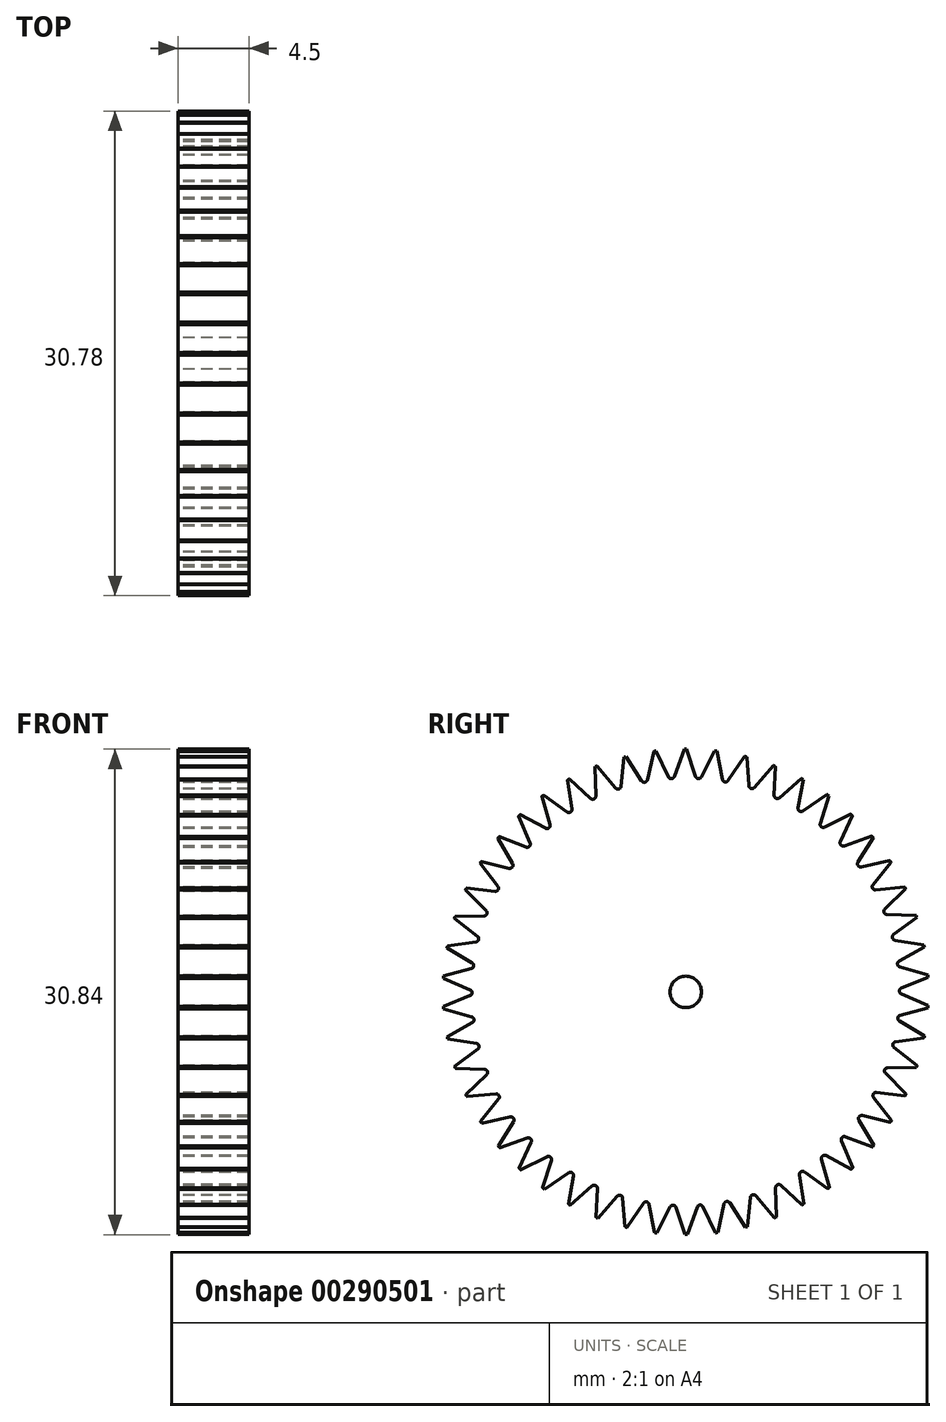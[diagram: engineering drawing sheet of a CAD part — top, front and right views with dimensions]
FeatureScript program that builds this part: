
annotation { "Feature Type Name" : "Feature", "Feature Type Description" : "" }
export const myFeature = defineFeature(function(context is Context, id is Id, definition is map)
    precondition{}
    {
        {
            var Q0;
            Q0=qCreatedBy(makeId("Top.planeOp"),FACE);
            var sketch = newSketch(context, id + "F0", { "sketchPlane" : qUnion([Q0])});
            skLineSegment(sketch, "E0", {"start": v(0, 3.41) * mm, "end": v(0, -3.75) * mm, "construction": true});
            skLineSegment(sketch, "E1", {"start": v(0, 9.42) * mm, "end": v(2.25, 9.42) * mm});
            skLineSegment(sketch, "E2", {"start": v(2.25, 9.42) * mm, "end": v(2.25, 4.42) * mm});
            skLineSegment(sketch, "E3", {"start": v(2.25, 4.42) * mm, "end": v(2.25, 4.42) * mm});
            skLineSegment(sketch, "E4", {"start": v(2.25, 4.42) * mm, "end": v(2.25, 0) * mm});
            skLineSegment(sketch, "E5", {"start": v(2.25, 0) * mm, "end": v(2.25, 0) * mm});
            skLineSegment(sketch, "E6", {"start": v(2.25, 0) * mm, "end": v(2.25, -5) * mm});
            skLineSegment(sketch, "E7", {"start": v(2.25, -5) * mm, "end": v(0, -5) * mm});
            skLineSegment(sketch, "E8.MirrorCS", {"start": v(-2.25, 0) * mm, "end": v(-2.25, 0) * mm});
            skLineSegment(sketch, "E9.MirrorCS", {"start": v(0, 9.42) * mm, "end": v(-2.25, 9.42) * mm});
            skLineSegment(sketch, "E10.MirrorCS", {"start": v(-2.25, -5) * mm, "end": v(0, -5) * mm});
            skLineSegment(sketch, "E11.MirrorCS", {"start": v(-2.25, 0) * mm, "end": v(-2.25, -5) * mm});
            skLineSegment(sketch, "E12.MirrorCS", {"start": v(-2.25, 9.42) * mm, "end": v(-2.25, 4.42) * mm});
            skLineSegment(sketch, "E13.MirrorCS", {"start": v(-2.25, 4.42) * mm, "end": v(-2.25, 0) * mm});
            skLineSegment(sketch, "E14.MirrorCS", {"start": v(-2.25, 4.42) * mm, "end": v(-2.25, 4.42) * mm});
            skLineSegment(sketch, "E15", {"start": v(-2.96, -6) * mm, "end": v(4.6, -6) * mm, "construction": true});
            skLineSegment(sketch, "E16.MirrorCS", {"start": v(-2.25, -12) * mm, "end": v(-2.25, -12) * mm});
            skLineSegment(sketch, "E17.MirrorCS", {"start": v(2.25, -12) * mm, "end": v(2.25, -12) * mm});
            skLineSegment(sketch, "E18.MirrorCS", {"start": v(-2.25, -16.42) * mm, "end": v(-2.25, -16.42) * mm});
            skLineSegment(sketch, "E19.MirrorCS", {"start": v(-2.25, -16.42) * mm, "end": v(-2.25, -12) * mm});
            skLineSegment(sketch, "E20.MirrorCS", {"start": v(-2.25, -21.42) * mm, "end": v(-2.25, -16.42) * mm});
            skLineSegment(sketch, "E21.MirrorCS", {"start": v(-2.25, -12) * mm, "end": v(-2.25, -7) * mm});
            skLineSegment(sketch, "E22.MirrorCS", {"start": v(-2.25, -7) * mm, "end": v(0, -7) * mm});
            skLineSegment(sketch, "E23.MirrorCS", {"start": v(0, -21.42) * mm, "end": v(-2.25, -21.42) * mm});
            skLineSegment(sketch, "E24.MirrorCS", {"start": v(2.25, -7) * mm, "end": v(0, -7) * mm});
            skLineSegment(sketch, "E25.MirrorCS", {"start": v(2.25, -21.42) * mm, "end": v(2.25, -16.42) * mm});
            skLineSegment(sketch, "E26.MirrorCS", {"start": v(2.25, -16.42) * mm, "end": v(2.25, -16.42) * mm});
            skLineSegment(sketch, "E27.MirrorCS", {"start": v(2.25, -12) * mm, "end": v(2.25, -7) * mm});
            skLineSegment(sketch, "E28.MirrorCS", {"start": v(2.25, -16.42) * mm, "end": v(2.25, -12) * mm});
            skLineSegment(sketch, "E29.MirrorCS", {"start": v(0, -21.42) * mm, "end": v(2.25, -21.42) * mm});
            skSolve(sketch);
        }
        {
            var Q0;
            Q0=makeQuery(id+"F0.imprint","IMPRINT",FACE,{"disambiguationData":[TD([[makeQuery(id+"F0.imprint","IMPRINT",EDGE,{"derivedFrom":sQuery(id+"F0.wireOp",EDGE,"E1")}),-1.0]])]});
            var Q1;
            Q1=sQuery(id+"F0.wireOp",EDGE,"E14.MirrorCS");
            var Q2;
            Q2=sQuery(id+"F0.wireOp",EDGE,"E13.MirrorCS");
            var Q3;
            Q3=sQuery(id+"F0.wireOp",EDGE,"E2");
            var Q4;
            Q4=sQuery(id+"F0.wireOp",EDGE,"E3");
            var Q5;
            Q5=sQuery(id+"F0.wireOp",EDGE,"E1");
            var Q6;
            Q6=sQuery(id+"F0.wireOp",EDGE,"E4");
            var Q7;
            Q7=sQuery(id+"F0.wireOp",EDGE,"E7");
            var Q8;
            Q8=sQuery(id+"F0.wireOp",EDGE,"E9.MirrorCS");
            var Q9;
            Q9=sQuery(id+"F0.wireOp",EDGE,"E10.MirrorCS");
            var Q10;
            Q10=sQuery(id+"F0.wireOp",EDGE,"E12.MirrorCS");
            var Q11;
            Q11=sQuery(id+"F0.wireOp",EDGE,"E5");
            var Q12;
            Q12=sQuery(id+"F0.wireOp",EDGE,"E6");
            var Q13;
            Q13=sQuery(id+"F0.wireOp",EDGE,"E8.MirrorCS");
            var Q14;
            Q14=sQuery(id+"F0.wireOp",EDGE,"E11.MirrorCS");
            var Q15;
            Q15=sQuery(id+"F0.wireOp",EDGE,"E15");
            revolve(context, id + "F1", {"entities" : qUnion([Q0]), "surfaceEntities" : qUnion([Q1, Q2, Q3, Q4, Q5, Q6, Q7, Q8, Q9, Q10, Q11, Q12, Q13, Q14]), "axis" : qUnion([Q15]), "revolveType" : RevolveType.FULL});
        }
        {
            var Q0;
            Q0=makeQuery(id+"F1.opRevolve","SWEPT_FACE",FACE,{"disambiguationData":[OSD([sQuery(id+"F0.wireOp",EDGE,"E12.MirrorCS")])]});
            var sketch = newSketch(context, id + "F2", { "sketchPlane" : qUnion([Q0])});
            skCircle(sketch, "E30.0", {"center": v(6, 0) * mm, "radius": 15.42 * mm});
            skCircle(sketch, "E30.1", {"center": v(6.5, 0) * mm, "radius": 10.92 * mm});
            skCircle(sketch, "E30.2", {"center": v(6, 0) * mm, "radius": 1 * mm});
            skLineSegment(sketch, "E31", {"start": v(6, 0) * mm, "end": v(21.39, 0.94) * mm});
            skLineSegment(sketch, "E32.1.0", {"start": v(6, 0) * mm, "end": v(21.15, 2.86) * mm});
            skLineSegment(sketch, "E32.2.0", {"start": v(6, 0) * mm, "end": v(20.67, 4.74) * mm});
            skLineSegment(sketch, "E32.3.0", {"start": v(6, 0) * mm, "end": v(19.96, 6.54) * mm});
            skLineSegment(sketch, "E32.4.0", {"start": v(6, 0) * mm, "end": v(19.03, 8.24) * mm});
            skLineSegment(sketch, "E32.5.0", {"start": v(6, 0) * mm, "end": v(17.9, 9.8) * mm});
            skLineSegment(sketch, "E32.6.0", {"start": v(6, 0) * mm, "end": v(16.57, 11.22) * mm});
            skLineSegment(sketch, "E32.7.0", {"start": v(6, 0) * mm, "end": v(15.08, 12.46) * mm});
            skLineSegment(sketch, "E32.8.0", {"start": v(6, 0) * mm, "end": v(13.45, 13.5) * mm});
            skLineSegment(sketch, "E32.9.0", {"start": v(6, 0) * mm, "end": v(11.7, 14.32) * mm});
            skLineSegment(sketch, "E32.10.0", {"start": v(6, 0) * mm, "end": v(9.86, 14.92) * mm});
            skLineSegment(sketch, "E32.11.0", {"start": v(6, 0) * mm, "end": v(7.96, 15.3) * mm});
            skLineSegment(sketch, "E32.12.0", {"start": v(6, 0) * mm, "end": v(6.03, 15.42) * mm});
            skLineSegment(sketch, "E32.13.0", {"start": v(6, 0) * mm, "end": v(4.1, 15.3) * mm});
            skLineSegment(sketch, "E32.14.0", {"start": v(6, 0) * mm, "end": v(2.2, 14.94) * mm});
            skLineSegment(sketch, "E32.15.0", {"start": v(6, 0) * mm, "end": v(0.35, 14.34) * mm});
            skLineSegment(sketch, "E32.16.0", {"start": v(6, 0) * mm, "end": v(-1.4, 13.52) * mm});
            skLineSegment(sketch, "E32.17.0", {"start": v(6, 0) * mm, "end": v(-3.04, 12.49) * mm});
            skLineSegment(sketch, "E32.18.0", {"start": v(6, 0) * mm, "end": v(-4.53, 11.25) * mm});
            skLineSegment(sketch, "E32.19.0", {"start": v(6, 0) * mm, "end": v(-5.86, 9.85) * mm});
            skLineSegment(sketch, "E32.20.0", {"start": v(6, 0) * mm, "end": v(-7, 8.28) * mm});
            skLineSegment(sketch, "E32.21.0", {"start": v(6, 0) * mm, "end": v(-7.94, 6.59) * mm});
            skLineSegment(sketch, "E32.22.0", {"start": v(6, 0) * mm, "end": v(-8.65, 4.79) * mm});
            skLineSegment(sketch, "E32.23.0", {"start": v(6, 0) * mm, "end": v(-9.14, 2.91) * mm});
            skLineSegment(sketch, "E32.24.0", {"start": v(6, 0) * mm, "end": v(-9.38, 1) * mm});
            skLineSegment(sketch, "E32.25.0", {"start": v(6, 0) * mm, "end": v(-9.39, -0.94) * mm});
            skLineSegment(sketch, "E32.26.0", {"start": v(6, 0) * mm, "end": v(-9.15, -2.86) * mm});
            skLineSegment(sketch, "E32.27.0", {"start": v(6, 0) * mm, "end": v(-8.67, -4.74) * mm});
            skLineSegment(sketch, "E32.28.0", {"start": v(6, 0) * mm, "end": v(-7.96, -6.54) * mm});
            skLineSegment(sketch, "E32.29.0", {"start": v(6, 0) * mm, "end": v(-7.03, -8.24) * mm});
            skLineSegment(sketch, "E32.30.0", {"start": v(6, 0) * mm, "end": v(-5.9, -9.8) * mm});
            skLineSegment(sketch, "E32.31.0", {"start": v(6, 0) * mm, "end": v(-4.57, -11.22) * mm});
            skLineSegment(sketch, "E32.32.0", {"start": v(6, 0) * mm, "end": v(-3.08, -12.46) * mm});
            skLineSegment(sketch, "E32.33.0", {"start": v(6, 0) * mm, "end": v(-1.45, -13.5) * mm});
            skLineSegment(sketch, "E32.34.0", {"start": v(6, 0) * mm, "end": v(0.3, -14.32) * mm});
            skLineSegment(sketch, "E32.35.0", {"start": v(6, 0) * mm, "end": v(2.14, -14.92) * mm});
            skLineSegment(sketch, "E32.36.0", {"start": v(6, 0) * mm, "end": v(4.04, -15.3) * mm});
            skLineSegment(sketch, "E32.37.0", {"start": v(6, 0) * mm, "end": v(5.97, -15.42) * mm});
            skLineSegment(sketch, "E32.38.0", {"start": v(6, 0) * mm, "end": v(7.9, -15.3) * mm});
            skLineSegment(sketch, "E32.39.0", {"start": v(6, 0) * mm, "end": v(9.8, -14.94) * mm});
            skLineSegment(sketch, "E32.40.0", {"start": v(6, 0) * mm, "end": v(11.65, -14.34) * mm});
            skLineSegment(sketch, "E32.41.0", {"start": v(6, 0) * mm, "end": v(13.4, -13.52) * mm});
            skLineSegment(sketch, "E32.42.0", {"start": v(6, 0) * mm, "end": v(15.04, -12.49) * mm});
            skLineSegment(sketch, "E32.43.0", {"start": v(6, 0) * mm, "end": v(16.53, -11.25) * mm});
            skLineSegment(sketch, "E32.44.0", {"start": v(6, 0) * mm, "end": v(17.86, -9.85) * mm});
            skLineSegment(sketch, "E32.45.0", {"start": v(6, 0) * mm, "end": v(19, -8.28) * mm});
            skLineSegment(sketch, "E32.46.0", {"start": v(6, 0) * mm, "end": v(19.94, -6.59) * mm});
            skLineSegment(sketch, "E32.47.0", {"start": v(6, 0) * mm, "end": v(20.65, -4.79) * mm});
            skLineSegment(sketch, "E32.48.0", {"start": v(6, 0) * mm, "end": v(21.14, -2.91) * mm});
            skLineSegment(sketch, "E32.49.0", {"start": v(6, 0) * mm, "end": v(21.38, -1) * mm});
            skCircle(sketch, "E33.0", {"center": v(6, 0) * mm, "radius": 15.62 * mm});
            skLineSegment(sketch, "E34", {"start": v(21.4, 2.91) * mm, "end": v(21.97, 3.02) * mm});
            skLineSegment(sketch, "E35", {"start": v(21.53, 0.95) * mm, "end": v(22.15, 0.99) * mm});
            skLineSegment(sketch, "E36", {"start": v(21.59, 0.96) * mm, "end": v(19.62, 1.48) * mm});
            skLineSegment(sketch, "E37", {"start": v(19.56, 1.84) * mm, "end": v(21.34, 2.9) * mm});
            skPoint(sketch, "E38.visualSharp", {"position": v(19.16, 1.6) * mm});
            skArc(sketch, "E38.filletArc", {"start": v(19.56, 1.84) * mm, "mid": v(19.47, 1.64) * mm, "end": v(19.62, 1.48) * mm});
            skSolve(sketch);
        }
        {
            var Q0;
            {var subQ5=sQuery(id+"F2.wireOp",EDGE,"E38.filletArc");Q0=makeQuery(id+"F2.imprint","IMPRINT",FACE,{"disambiguationData":[TD([[makeQuery(id+"F2.imprint","IMPRINT",EDGE,{"derivedFrom":subQ5}),1.0]])]});}
            extrude(context, id + "F3", {"entities" : qUnion([Q0]), "oppositeDirection" : true, "depth" : 5.73 * mm});
        }
        {
            var Q0;
            Q0=makeQuery(id+"F3.opExtrude","SWEPT_BODY",BODY,{"disambiguationData":[OSD([sQuery(id+"F2.wireOp",EDGE,"E30.0"),sQuery(id+"F2.wireOp",EDGE,"ktQJATyX-SdxZ-rI7u-VDDm-4vrzMGlF9boW"),sQuery(id+"F2.wireOp",EDGE,"HHLsh4HS-uaBy-oQPs-1Epk-ZBBctw4owGZm"),sQuery(id+"F2.wireOp",EDGE,"51925430-38b8-44a9-8ce9-339719db00ad.filletArc")])]});
            var Q1;
            Q1=makeQuery(id+"F1.opRevolve","SWEPT_EDGE",EDGE,{"disambiguationData":[OSD([sQuery(id+"F0.wireOp",EDGE,"E12.MirrorCS"),sQuery(id+"F0.wireOp",EDGE,"E14.MirrorCS")])]});
            circularPattern(context, id + "F4", {"entities" : qUnion([Q0]), "axis" : qUnion([Q1]), "angle" : 360 * degree, "instanceCount" : 50, "equalSpace" : true});
        }
        {
            var Q0;
            Q0=makeQuery(id+"F3.opExtrude","SWEPT_BODY",BODY,{"disambiguationData":[OSD([sQuery(id+"F2.wireOp",EDGE,"E30.0"),sQuery(id+"F2.wireOp",EDGE,"ktQJATyX-SdxZ-rI7u-VDDm-4vrzMGlF9boW"),sQuery(id+"F2.wireOp",EDGE,"HHLsh4HS-uaBy-oQPs-1Epk-ZBBctw4owGZm"),sQuery(id+"F2.wireOp",EDGE,"51925430-38b8-44a9-8ce9-339719db00ad.filletArc")])]});
            var Q1;
            Q1=makeQuery(id+"F4.opPattern","COPY",BODY,{"derivedFrom":makeQuery(id+"F3.opExtrude","SWEPT_BODY",BODY,{"disambiguationData":[OSD([sQuery(id+"F2.wireOp",EDGE,"E30.0"),sQuery(id+"F2.wireOp",EDGE,"ktQJATyX-SdxZ-rI7u-VDDm-4vrzMGlF9boW"),sQuery(id+"F2.wireOp",EDGE,"HHLsh4HS-uaBy-oQPs-1Epk-ZBBctw4owGZm"),sQuery(id+"F2.wireOp",EDGE,"51925430-38b8-44a9-8ce9-339719db00ad.filletArc")])]}),"instanceName":"1"});
            var Q2;
            Q2=makeQuery(id+"F4.opPattern","COPY",BODY,{"derivedFrom":makeQuery(id+"F3.opExtrude","SWEPT_BODY",BODY,{"disambiguationData":[OSD([sQuery(id+"F2.wireOp",EDGE,"E30.0"),sQuery(id+"F2.wireOp",EDGE,"ktQJATyX-SdxZ-rI7u-VDDm-4vrzMGlF9boW"),sQuery(id+"F2.wireOp",EDGE,"HHLsh4HS-uaBy-oQPs-1Epk-ZBBctw4owGZm"),sQuery(id+"F2.wireOp",EDGE,"51925430-38b8-44a9-8ce9-339719db00ad.filletArc")])]}),"instanceName":"2"});
            var Q3;
            Q3=makeQuery(id+"F4.opPattern","COPY",BODY,{"derivedFrom":makeQuery(id+"F3.opExtrude","SWEPT_BODY",BODY,{"disambiguationData":[OSD([sQuery(id+"F2.wireOp",EDGE,"E30.0"),sQuery(id+"F2.wireOp",EDGE,"ktQJATyX-SdxZ-rI7u-VDDm-4vrzMGlF9boW"),sQuery(id+"F2.wireOp",EDGE,"HHLsh4HS-uaBy-oQPs-1Epk-ZBBctw4owGZm"),sQuery(id+"F2.wireOp",EDGE,"51925430-38b8-44a9-8ce9-339719db00ad.filletArc")])]}),"instanceName":"3"});
            var Q4;
            Q4=makeQuery(id+"F4.opPattern","COPY",BODY,{"derivedFrom":makeQuery(id+"F3.opExtrude","SWEPT_BODY",BODY,{"disambiguationData":[OSD([sQuery(id+"F2.wireOp",EDGE,"E30.0"),sQuery(id+"F2.wireOp",EDGE,"ktQJATyX-SdxZ-rI7u-VDDm-4vrzMGlF9boW"),sQuery(id+"F2.wireOp",EDGE,"HHLsh4HS-uaBy-oQPs-1Epk-ZBBctw4owGZm"),sQuery(id+"F2.wireOp",EDGE,"51925430-38b8-44a9-8ce9-339719db00ad.filletArc")])]}),"instanceName":"4"});
            var Q5;
            Q5=makeQuery(id+"F4.opPattern","COPY",BODY,{"derivedFrom":makeQuery(id+"F3.opExtrude","SWEPT_BODY",BODY,{"disambiguationData":[OSD([sQuery(id+"F2.wireOp",EDGE,"E30.0"),sQuery(id+"F2.wireOp",EDGE,"ktQJATyX-SdxZ-rI7u-VDDm-4vrzMGlF9boW"),sQuery(id+"F2.wireOp",EDGE,"HHLsh4HS-uaBy-oQPs-1Epk-ZBBctw4owGZm"),sQuery(id+"F2.wireOp",EDGE,"51925430-38b8-44a9-8ce9-339719db00ad.filletArc")])]}),"instanceName":"5"});
            var Q6;
            Q6=makeQuery(id+"F4.opPattern","COPY",BODY,{"derivedFrom":makeQuery(id+"F3.opExtrude","SWEPT_BODY",BODY,{"disambiguationData":[OSD([sQuery(id+"F2.wireOp",EDGE,"E30.0"),sQuery(id+"F2.wireOp",EDGE,"ktQJATyX-SdxZ-rI7u-VDDm-4vrzMGlF9boW"),sQuery(id+"F2.wireOp",EDGE,"HHLsh4HS-uaBy-oQPs-1Epk-ZBBctw4owGZm"),sQuery(id+"F2.wireOp",EDGE,"51925430-38b8-44a9-8ce9-339719db00ad.filletArc")])]}),"instanceName":"6"});
            var Q7;
            Q7=makeQuery(id+"F4.opPattern","COPY",BODY,{"derivedFrom":makeQuery(id+"F3.opExtrude","SWEPT_BODY",BODY,{"disambiguationData":[OSD([sQuery(id+"F2.wireOp",EDGE,"E30.0"),sQuery(id+"F2.wireOp",EDGE,"ktQJATyX-SdxZ-rI7u-VDDm-4vrzMGlF9boW"),sQuery(id+"F2.wireOp",EDGE,"HHLsh4HS-uaBy-oQPs-1Epk-ZBBctw4owGZm"),sQuery(id+"F2.wireOp",EDGE,"51925430-38b8-44a9-8ce9-339719db00ad.filletArc")])]}),"instanceName":"7"});
            var Q8;
            Q8=makeQuery(id+"F4.opPattern","COPY",BODY,{"derivedFrom":makeQuery(id+"F3.opExtrude","SWEPT_BODY",BODY,{"disambiguationData":[OSD([sQuery(id+"F2.wireOp",EDGE,"E30.0"),sQuery(id+"F2.wireOp",EDGE,"ktQJATyX-SdxZ-rI7u-VDDm-4vrzMGlF9boW"),sQuery(id+"F2.wireOp",EDGE,"HHLsh4HS-uaBy-oQPs-1Epk-ZBBctw4owGZm"),sQuery(id+"F2.wireOp",EDGE,"51925430-38b8-44a9-8ce9-339719db00ad.filletArc")])]}),"instanceName":"8"});
            var Q9;
            Q9=makeQuery(id+"F4.opPattern","COPY",BODY,{"derivedFrom":makeQuery(id+"F3.opExtrude","SWEPT_BODY",BODY,{"disambiguationData":[OSD([sQuery(id+"F2.wireOp",EDGE,"E30.0"),sQuery(id+"F2.wireOp",EDGE,"ktQJATyX-SdxZ-rI7u-VDDm-4vrzMGlF9boW"),sQuery(id+"F2.wireOp",EDGE,"HHLsh4HS-uaBy-oQPs-1Epk-ZBBctw4owGZm"),sQuery(id+"F2.wireOp",EDGE,"51925430-38b8-44a9-8ce9-339719db00ad.filletArc")])]}),"instanceName":"9"});
            var Q10;
            Q10=makeQuery(id+"F4.opPattern","COPY",BODY,{"derivedFrom":makeQuery(id+"F3.opExtrude","SWEPT_BODY",BODY,{"disambiguationData":[OSD([sQuery(id+"F2.wireOp",EDGE,"E30.0"),sQuery(id+"F2.wireOp",EDGE,"ktQJATyX-SdxZ-rI7u-VDDm-4vrzMGlF9boW"),sQuery(id+"F2.wireOp",EDGE,"HHLsh4HS-uaBy-oQPs-1Epk-ZBBctw4owGZm"),sQuery(id+"F2.wireOp",EDGE,"51925430-38b8-44a9-8ce9-339719db00ad.filletArc")])]}),"instanceName":"10"});
            var Q11;
            Q11=makeQuery(id+"F4.opPattern","COPY",BODY,{"derivedFrom":makeQuery(id+"F3.opExtrude","SWEPT_BODY",BODY,{"disambiguationData":[OSD([sQuery(id+"F2.wireOp",EDGE,"E30.0"),sQuery(id+"F2.wireOp",EDGE,"ktQJATyX-SdxZ-rI7u-VDDm-4vrzMGlF9boW"),sQuery(id+"F2.wireOp",EDGE,"HHLsh4HS-uaBy-oQPs-1Epk-ZBBctw4owGZm"),sQuery(id+"F2.wireOp",EDGE,"51925430-38b8-44a9-8ce9-339719db00ad.filletArc")])]}),"instanceName":"11"});
            var Q12;
            Q12=makeQuery(id+"F4.opPattern","COPY",BODY,{"derivedFrom":makeQuery(id+"F3.opExtrude","SWEPT_BODY",BODY,{"disambiguationData":[OSD([sQuery(id+"F2.wireOp",EDGE,"E30.0"),sQuery(id+"F2.wireOp",EDGE,"ktQJATyX-SdxZ-rI7u-VDDm-4vrzMGlF9boW"),sQuery(id+"F2.wireOp",EDGE,"HHLsh4HS-uaBy-oQPs-1Epk-ZBBctw4owGZm"),sQuery(id+"F2.wireOp",EDGE,"51925430-38b8-44a9-8ce9-339719db00ad.filletArc")])]}),"instanceName":"12"});
            var Q13;
            Q13=makeQuery(id+"F4.opPattern","COPY",BODY,{"derivedFrom":makeQuery(id+"F3.opExtrude","SWEPT_BODY",BODY,{"disambiguationData":[OSD([sQuery(id+"F2.wireOp",EDGE,"E30.0"),sQuery(id+"F2.wireOp",EDGE,"ktQJATyX-SdxZ-rI7u-VDDm-4vrzMGlF9boW"),sQuery(id+"F2.wireOp",EDGE,"HHLsh4HS-uaBy-oQPs-1Epk-ZBBctw4owGZm"),sQuery(id+"F2.wireOp",EDGE,"51925430-38b8-44a9-8ce9-339719db00ad.filletArc")])]}),"instanceName":"13"});
            var Q14;
            Q14=makeQuery(id+"F4.opPattern","COPY",BODY,{"derivedFrom":makeQuery(id+"F3.opExtrude","SWEPT_BODY",BODY,{"disambiguationData":[OSD([sQuery(id+"F2.wireOp",EDGE,"E30.0"),sQuery(id+"F2.wireOp",EDGE,"ktQJATyX-SdxZ-rI7u-VDDm-4vrzMGlF9boW"),sQuery(id+"F2.wireOp",EDGE,"HHLsh4HS-uaBy-oQPs-1Epk-ZBBctw4owGZm"),sQuery(id+"F2.wireOp",EDGE,"51925430-38b8-44a9-8ce9-339719db00ad.filletArc")])]}),"instanceName":"14"});
            var Q15;
            Q15=makeQuery(id+"F4.opPattern","COPY",BODY,{"derivedFrom":makeQuery(id+"F3.opExtrude","SWEPT_BODY",BODY,{"disambiguationData":[OSD([sQuery(id+"F2.wireOp",EDGE,"E30.0"),sQuery(id+"F2.wireOp",EDGE,"ktQJATyX-SdxZ-rI7u-VDDm-4vrzMGlF9boW"),sQuery(id+"F2.wireOp",EDGE,"HHLsh4HS-uaBy-oQPs-1Epk-ZBBctw4owGZm"),sQuery(id+"F2.wireOp",EDGE,"51925430-38b8-44a9-8ce9-339719db00ad.filletArc")])]}),"instanceName":"15"});
            var Q16;
            Q16=makeQuery(id+"F4.opPattern","COPY",BODY,{"derivedFrom":makeQuery(id+"F3.opExtrude","SWEPT_BODY",BODY,{"disambiguationData":[OSD([sQuery(id+"F2.wireOp",EDGE,"E30.0"),sQuery(id+"F2.wireOp",EDGE,"ktQJATyX-SdxZ-rI7u-VDDm-4vrzMGlF9boW"),sQuery(id+"F2.wireOp",EDGE,"HHLsh4HS-uaBy-oQPs-1Epk-ZBBctw4owGZm"),sQuery(id+"F2.wireOp",EDGE,"51925430-38b8-44a9-8ce9-339719db00ad.filletArc")])]}),"instanceName":"16"});
            var Q17;
            Q17=makeQuery(id+"F4.opPattern","COPY",BODY,{"derivedFrom":makeQuery(id+"F3.opExtrude","SWEPT_BODY",BODY,{"disambiguationData":[OSD([sQuery(id+"F2.wireOp",EDGE,"E30.0"),sQuery(id+"F2.wireOp",EDGE,"ktQJATyX-SdxZ-rI7u-VDDm-4vrzMGlF9boW"),sQuery(id+"F2.wireOp",EDGE,"HHLsh4HS-uaBy-oQPs-1Epk-ZBBctw4owGZm"),sQuery(id+"F2.wireOp",EDGE,"51925430-38b8-44a9-8ce9-339719db00ad.filletArc")])]}),"instanceName":"17"});
            var Q18;
            Q18=makeQuery(id+"F4.opPattern","COPY",BODY,{"derivedFrom":makeQuery(id+"F3.opExtrude","SWEPT_BODY",BODY,{"disambiguationData":[OSD([sQuery(id+"F2.wireOp",EDGE,"E30.0"),sQuery(id+"F2.wireOp",EDGE,"ktQJATyX-SdxZ-rI7u-VDDm-4vrzMGlF9boW"),sQuery(id+"F2.wireOp",EDGE,"HHLsh4HS-uaBy-oQPs-1Epk-ZBBctw4owGZm"),sQuery(id+"F2.wireOp",EDGE,"51925430-38b8-44a9-8ce9-339719db00ad.filletArc")])]}),"instanceName":"18"});
            var Q19;
            Q19=makeQuery(id+"F4.opPattern","COPY",BODY,{"derivedFrom":makeQuery(id+"F3.opExtrude","SWEPT_BODY",BODY,{"disambiguationData":[OSD([sQuery(id+"F2.wireOp",EDGE,"E30.0"),sQuery(id+"F2.wireOp",EDGE,"ktQJATyX-SdxZ-rI7u-VDDm-4vrzMGlF9boW"),sQuery(id+"F2.wireOp",EDGE,"HHLsh4HS-uaBy-oQPs-1Epk-ZBBctw4owGZm"),sQuery(id+"F2.wireOp",EDGE,"51925430-38b8-44a9-8ce9-339719db00ad.filletArc")])]}),"instanceName":"19"});
            var Q20;
            Q20=makeQuery(id+"F4.opPattern","COPY",BODY,{"derivedFrom":makeQuery(id+"F3.opExtrude","SWEPT_BODY",BODY,{"disambiguationData":[OSD([sQuery(id+"F2.wireOp",EDGE,"E30.0"),sQuery(id+"F2.wireOp",EDGE,"ktQJATyX-SdxZ-rI7u-VDDm-4vrzMGlF9boW"),sQuery(id+"F2.wireOp",EDGE,"HHLsh4HS-uaBy-oQPs-1Epk-ZBBctw4owGZm"),sQuery(id+"F2.wireOp",EDGE,"51925430-38b8-44a9-8ce9-339719db00ad.filletArc")])]}),"instanceName":"20"});
            var Q21;
            Q21=makeQuery(id+"F4.opPattern","COPY",BODY,{"derivedFrom":makeQuery(id+"F3.opExtrude","SWEPT_BODY",BODY,{"disambiguationData":[OSD([sQuery(id+"F2.wireOp",EDGE,"E30.0"),sQuery(id+"F2.wireOp",EDGE,"ktQJATyX-SdxZ-rI7u-VDDm-4vrzMGlF9boW"),sQuery(id+"F2.wireOp",EDGE,"HHLsh4HS-uaBy-oQPs-1Epk-ZBBctw4owGZm"),sQuery(id+"F2.wireOp",EDGE,"51925430-38b8-44a9-8ce9-339719db00ad.filletArc")])]}),"instanceName":"21"});
            var Q22;
            Q22=makeQuery(id+"F4.opPattern","COPY",BODY,{"derivedFrom":makeQuery(id+"F3.opExtrude","SWEPT_BODY",BODY,{"disambiguationData":[OSD([sQuery(id+"F2.wireOp",EDGE,"E30.0"),sQuery(id+"F2.wireOp",EDGE,"ktQJATyX-SdxZ-rI7u-VDDm-4vrzMGlF9boW"),sQuery(id+"F2.wireOp",EDGE,"HHLsh4HS-uaBy-oQPs-1Epk-ZBBctw4owGZm"),sQuery(id+"F2.wireOp",EDGE,"51925430-38b8-44a9-8ce9-339719db00ad.filletArc")])]}),"instanceName":"22"});
            var Q23;
            Q23=makeQuery(id+"F4.opPattern","COPY",BODY,{"derivedFrom":makeQuery(id+"F3.opExtrude","SWEPT_BODY",BODY,{"disambiguationData":[OSD([sQuery(id+"F2.wireOp",EDGE,"E30.0"),sQuery(id+"F2.wireOp",EDGE,"ktQJATyX-SdxZ-rI7u-VDDm-4vrzMGlF9boW"),sQuery(id+"F2.wireOp",EDGE,"HHLsh4HS-uaBy-oQPs-1Epk-ZBBctw4owGZm"),sQuery(id+"F2.wireOp",EDGE,"51925430-38b8-44a9-8ce9-339719db00ad.filletArc")])]}),"instanceName":"23"});
            var Q24;
            Q24=makeQuery(id+"F4.opPattern","COPY",BODY,{"derivedFrom":makeQuery(id+"F3.opExtrude","SWEPT_BODY",BODY,{"disambiguationData":[OSD([sQuery(id+"F2.wireOp",EDGE,"E30.0"),sQuery(id+"F2.wireOp",EDGE,"ktQJATyX-SdxZ-rI7u-VDDm-4vrzMGlF9boW"),sQuery(id+"F2.wireOp",EDGE,"HHLsh4HS-uaBy-oQPs-1Epk-ZBBctw4owGZm"),sQuery(id+"F2.wireOp",EDGE,"51925430-38b8-44a9-8ce9-339719db00ad.filletArc")])]}),"instanceName":"24"});
            var Q25;
            Q25=makeQuery(id+"F4.opPattern","COPY",BODY,{"derivedFrom":makeQuery(id+"F3.opExtrude","SWEPT_BODY",BODY,{"disambiguationData":[OSD([sQuery(id+"F2.wireOp",EDGE,"E30.0"),sQuery(id+"F2.wireOp",EDGE,"ktQJATyX-SdxZ-rI7u-VDDm-4vrzMGlF9boW"),sQuery(id+"F2.wireOp",EDGE,"HHLsh4HS-uaBy-oQPs-1Epk-ZBBctw4owGZm"),sQuery(id+"F2.wireOp",EDGE,"51925430-38b8-44a9-8ce9-339719db00ad.filletArc")])]}),"instanceName":"25"});
            var Q26;
            Q26=makeQuery(id+"F4.opPattern","COPY",BODY,{"derivedFrom":makeQuery(id+"F3.opExtrude","SWEPT_BODY",BODY,{"disambiguationData":[OSD([sQuery(id+"F2.wireOp",EDGE,"E30.0"),sQuery(id+"F2.wireOp",EDGE,"ktQJATyX-SdxZ-rI7u-VDDm-4vrzMGlF9boW"),sQuery(id+"F2.wireOp",EDGE,"HHLsh4HS-uaBy-oQPs-1Epk-ZBBctw4owGZm"),sQuery(id+"F2.wireOp",EDGE,"51925430-38b8-44a9-8ce9-339719db00ad.filletArc")])]}),"instanceName":"26"});
            var Q27;
            Q27=makeQuery(id+"F4.opPattern","COPY",BODY,{"derivedFrom":makeQuery(id+"F3.opExtrude","SWEPT_BODY",BODY,{"disambiguationData":[OSD([sQuery(id+"F2.wireOp",EDGE,"E30.0"),sQuery(id+"F2.wireOp",EDGE,"ktQJATyX-SdxZ-rI7u-VDDm-4vrzMGlF9boW"),sQuery(id+"F2.wireOp",EDGE,"HHLsh4HS-uaBy-oQPs-1Epk-ZBBctw4owGZm"),sQuery(id+"F2.wireOp",EDGE,"51925430-38b8-44a9-8ce9-339719db00ad.filletArc")])]}),"instanceName":"27"});
            var Q28;
            Q28=makeQuery(id+"F4.opPattern","COPY",BODY,{"derivedFrom":makeQuery(id+"F3.opExtrude","SWEPT_BODY",BODY,{"disambiguationData":[OSD([sQuery(id+"F2.wireOp",EDGE,"E30.0"),sQuery(id+"F2.wireOp",EDGE,"ktQJATyX-SdxZ-rI7u-VDDm-4vrzMGlF9boW"),sQuery(id+"F2.wireOp",EDGE,"HHLsh4HS-uaBy-oQPs-1Epk-ZBBctw4owGZm"),sQuery(id+"F2.wireOp",EDGE,"51925430-38b8-44a9-8ce9-339719db00ad.filletArc")])]}),"instanceName":"28"});
            var Q29;
            Q29=makeQuery(id+"F4.opPattern","COPY",BODY,{"derivedFrom":makeQuery(id+"F3.opExtrude","SWEPT_BODY",BODY,{"disambiguationData":[OSD([sQuery(id+"F2.wireOp",EDGE,"E30.0"),sQuery(id+"F2.wireOp",EDGE,"ktQJATyX-SdxZ-rI7u-VDDm-4vrzMGlF9boW"),sQuery(id+"F2.wireOp",EDGE,"HHLsh4HS-uaBy-oQPs-1Epk-ZBBctw4owGZm"),sQuery(id+"F2.wireOp",EDGE,"51925430-38b8-44a9-8ce9-339719db00ad.filletArc")])]}),"instanceName":"29"});
            var Q30;
            Q30=makeQuery(id+"F4.opPattern","COPY",BODY,{"derivedFrom":makeQuery(id+"F3.opExtrude","SWEPT_BODY",BODY,{"disambiguationData":[OSD([sQuery(id+"F2.wireOp",EDGE,"E30.0"),sQuery(id+"F2.wireOp",EDGE,"ktQJATyX-SdxZ-rI7u-VDDm-4vrzMGlF9boW"),sQuery(id+"F2.wireOp",EDGE,"HHLsh4HS-uaBy-oQPs-1Epk-ZBBctw4owGZm"),sQuery(id+"F2.wireOp",EDGE,"51925430-38b8-44a9-8ce9-339719db00ad.filletArc")])]}),"instanceName":"30"});
            var Q31;
            Q31=makeQuery(id+"F4.opPattern","COPY",BODY,{"derivedFrom":makeQuery(id+"F3.opExtrude","SWEPT_BODY",BODY,{"disambiguationData":[OSD([sQuery(id+"F2.wireOp",EDGE,"E30.0"),sQuery(id+"F2.wireOp",EDGE,"ktQJATyX-SdxZ-rI7u-VDDm-4vrzMGlF9boW"),sQuery(id+"F2.wireOp",EDGE,"HHLsh4HS-uaBy-oQPs-1Epk-ZBBctw4owGZm"),sQuery(id+"F2.wireOp",EDGE,"51925430-38b8-44a9-8ce9-339719db00ad.filletArc")])]}),"instanceName":"31"});
            var Q32;
            Q32=makeQuery(id+"F4.opPattern","COPY",BODY,{"derivedFrom":makeQuery(id+"F3.opExtrude","SWEPT_BODY",BODY,{"disambiguationData":[OSD([sQuery(id+"F2.wireOp",EDGE,"E30.0"),sQuery(id+"F2.wireOp",EDGE,"ktQJATyX-SdxZ-rI7u-VDDm-4vrzMGlF9boW"),sQuery(id+"F2.wireOp",EDGE,"HHLsh4HS-uaBy-oQPs-1Epk-ZBBctw4owGZm"),sQuery(id+"F2.wireOp",EDGE,"51925430-38b8-44a9-8ce9-339719db00ad.filletArc")])]}),"instanceName":"32"});
            var Q33;
            Q33=makeQuery(id+"F4.opPattern","COPY",BODY,{"derivedFrom":makeQuery(id+"F3.opExtrude","SWEPT_BODY",BODY,{"disambiguationData":[OSD([sQuery(id+"F2.wireOp",EDGE,"E30.0"),sQuery(id+"F2.wireOp",EDGE,"ktQJATyX-SdxZ-rI7u-VDDm-4vrzMGlF9boW"),sQuery(id+"F2.wireOp",EDGE,"HHLsh4HS-uaBy-oQPs-1Epk-ZBBctw4owGZm"),sQuery(id+"F2.wireOp",EDGE,"51925430-38b8-44a9-8ce9-339719db00ad.filletArc")])]}),"instanceName":"33"});
            var Q34;
            Q34=makeQuery(id+"F4.opPattern","COPY",BODY,{"derivedFrom":makeQuery(id+"F3.opExtrude","SWEPT_BODY",BODY,{"disambiguationData":[OSD([sQuery(id+"F2.wireOp",EDGE,"E30.0"),sQuery(id+"F2.wireOp",EDGE,"ktQJATyX-SdxZ-rI7u-VDDm-4vrzMGlF9boW"),sQuery(id+"F2.wireOp",EDGE,"HHLsh4HS-uaBy-oQPs-1Epk-ZBBctw4owGZm"),sQuery(id+"F2.wireOp",EDGE,"51925430-38b8-44a9-8ce9-339719db00ad.filletArc")])]}),"instanceName":"34"});
            var Q35;
            Q35=makeQuery(id+"F4.opPattern","COPY",BODY,{"derivedFrom":makeQuery(id+"F3.opExtrude","SWEPT_BODY",BODY,{"disambiguationData":[OSD([sQuery(id+"F2.wireOp",EDGE,"E30.0"),sQuery(id+"F2.wireOp",EDGE,"ktQJATyX-SdxZ-rI7u-VDDm-4vrzMGlF9boW"),sQuery(id+"F2.wireOp",EDGE,"HHLsh4HS-uaBy-oQPs-1Epk-ZBBctw4owGZm"),sQuery(id+"F2.wireOp",EDGE,"51925430-38b8-44a9-8ce9-339719db00ad.filletArc")])]}),"instanceName":"35"});
            var Q36;
            Q36=makeQuery(id+"F4.opPattern","COPY",BODY,{"derivedFrom":makeQuery(id+"F3.opExtrude","SWEPT_BODY",BODY,{"disambiguationData":[OSD([sQuery(id+"F2.wireOp",EDGE,"E30.0"),sQuery(id+"F2.wireOp",EDGE,"ktQJATyX-SdxZ-rI7u-VDDm-4vrzMGlF9boW"),sQuery(id+"F2.wireOp",EDGE,"HHLsh4HS-uaBy-oQPs-1Epk-ZBBctw4owGZm"),sQuery(id+"F2.wireOp",EDGE,"51925430-38b8-44a9-8ce9-339719db00ad.filletArc")])]}),"instanceName":"36"});
            var Q37;
            Q37=makeQuery(id+"F4.opPattern","COPY",BODY,{"derivedFrom":makeQuery(id+"F3.opExtrude","SWEPT_BODY",BODY,{"disambiguationData":[OSD([sQuery(id+"F2.wireOp",EDGE,"E30.0"),sQuery(id+"F2.wireOp",EDGE,"ktQJATyX-SdxZ-rI7u-VDDm-4vrzMGlF9boW"),sQuery(id+"F2.wireOp",EDGE,"HHLsh4HS-uaBy-oQPs-1Epk-ZBBctw4owGZm"),sQuery(id+"F2.wireOp",EDGE,"51925430-38b8-44a9-8ce9-339719db00ad.filletArc")])]}),"instanceName":"37"});
            var Q38;
            Q38=makeQuery(id+"F4.opPattern","COPY",BODY,{"derivedFrom":makeQuery(id+"F3.opExtrude","SWEPT_BODY",BODY,{"disambiguationData":[OSD([sQuery(id+"F2.wireOp",EDGE,"E30.0"),sQuery(id+"F2.wireOp",EDGE,"ktQJATyX-SdxZ-rI7u-VDDm-4vrzMGlF9boW"),sQuery(id+"F2.wireOp",EDGE,"HHLsh4HS-uaBy-oQPs-1Epk-ZBBctw4owGZm"),sQuery(id+"F2.wireOp",EDGE,"51925430-38b8-44a9-8ce9-339719db00ad.filletArc")])]}),"instanceName":"38"});
            var Q39;
            Q39=makeQuery(id+"F4.opPattern","COPY",BODY,{"derivedFrom":makeQuery(id+"F3.opExtrude","SWEPT_BODY",BODY,{"disambiguationData":[OSD([sQuery(id+"F2.wireOp",EDGE,"E30.0"),sQuery(id+"F2.wireOp",EDGE,"ktQJATyX-SdxZ-rI7u-VDDm-4vrzMGlF9boW"),sQuery(id+"F2.wireOp",EDGE,"HHLsh4HS-uaBy-oQPs-1Epk-ZBBctw4owGZm"),sQuery(id+"F2.wireOp",EDGE,"51925430-38b8-44a9-8ce9-339719db00ad.filletArc")])]}),"instanceName":"39"});
            var Q40;
            Q40=makeQuery(id+"F4.opPattern","COPY",BODY,{"derivedFrom":makeQuery(id+"F3.opExtrude","SWEPT_BODY",BODY,{"disambiguationData":[OSD([sQuery(id+"F2.wireOp",EDGE,"E30.0"),sQuery(id+"F2.wireOp",EDGE,"ktQJATyX-SdxZ-rI7u-VDDm-4vrzMGlF9boW"),sQuery(id+"F2.wireOp",EDGE,"HHLsh4HS-uaBy-oQPs-1Epk-ZBBctw4owGZm"),sQuery(id+"F2.wireOp",EDGE,"51925430-38b8-44a9-8ce9-339719db00ad.filletArc")])]}),"instanceName":"40"});
            var Q41;
            Q41=makeQuery(id+"F4.opPattern","COPY",BODY,{"derivedFrom":makeQuery(id+"F3.opExtrude","SWEPT_BODY",BODY,{"disambiguationData":[OSD([sQuery(id+"F2.wireOp",EDGE,"E30.0"),sQuery(id+"F2.wireOp",EDGE,"ktQJATyX-SdxZ-rI7u-VDDm-4vrzMGlF9boW"),sQuery(id+"F2.wireOp",EDGE,"HHLsh4HS-uaBy-oQPs-1Epk-ZBBctw4owGZm"),sQuery(id+"F2.wireOp",EDGE,"51925430-38b8-44a9-8ce9-339719db00ad.filletArc")])]}),"instanceName":"41"});
            var Q42;
            Q42=makeQuery(id+"F4.opPattern","COPY",BODY,{"derivedFrom":makeQuery(id+"F3.opExtrude","SWEPT_BODY",BODY,{"disambiguationData":[OSD([sQuery(id+"F2.wireOp",EDGE,"E30.0"),sQuery(id+"F2.wireOp",EDGE,"ktQJATyX-SdxZ-rI7u-VDDm-4vrzMGlF9boW"),sQuery(id+"F2.wireOp",EDGE,"HHLsh4HS-uaBy-oQPs-1Epk-ZBBctw4owGZm"),sQuery(id+"F2.wireOp",EDGE,"51925430-38b8-44a9-8ce9-339719db00ad.filletArc")])]}),"instanceName":"42"});
            var Q43;
            Q43=makeQuery(id+"F4.opPattern","COPY",BODY,{"derivedFrom":makeQuery(id+"F3.opExtrude","SWEPT_BODY",BODY,{"disambiguationData":[OSD([sQuery(id+"F2.wireOp",EDGE,"E30.0"),sQuery(id+"F2.wireOp",EDGE,"ktQJATyX-SdxZ-rI7u-VDDm-4vrzMGlF9boW"),sQuery(id+"F2.wireOp",EDGE,"HHLsh4HS-uaBy-oQPs-1Epk-ZBBctw4owGZm"),sQuery(id+"F2.wireOp",EDGE,"51925430-38b8-44a9-8ce9-339719db00ad.filletArc")])]}),"instanceName":"43"});
            var Q44;
            Q44=makeQuery(id+"F4.opPattern","COPY",BODY,{"derivedFrom":makeQuery(id+"F3.opExtrude","SWEPT_BODY",BODY,{"disambiguationData":[OSD([sQuery(id+"F2.wireOp",EDGE,"E30.0"),sQuery(id+"F2.wireOp",EDGE,"ktQJATyX-SdxZ-rI7u-VDDm-4vrzMGlF9boW"),sQuery(id+"F2.wireOp",EDGE,"HHLsh4HS-uaBy-oQPs-1Epk-ZBBctw4owGZm"),sQuery(id+"F2.wireOp",EDGE,"51925430-38b8-44a9-8ce9-339719db00ad.filletArc")])]}),"instanceName":"44"});
            var Q45;
            Q45=makeQuery(id+"F4.opPattern","COPY",BODY,{"derivedFrom":makeQuery(id+"F3.opExtrude","SWEPT_BODY",BODY,{"disambiguationData":[OSD([sQuery(id+"F2.wireOp",EDGE,"E30.0"),sQuery(id+"F2.wireOp",EDGE,"ktQJATyX-SdxZ-rI7u-VDDm-4vrzMGlF9boW"),sQuery(id+"F2.wireOp",EDGE,"HHLsh4HS-uaBy-oQPs-1Epk-ZBBctw4owGZm"),sQuery(id+"F2.wireOp",EDGE,"51925430-38b8-44a9-8ce9-339719db00ad.filletArc")])]}),"instanceName":"45"});
            var Q46;
            Q46=makeQuery(id+"F4.opPattern","COPY",BODY,{"derivedFrom":makeQuery(id+"F3.opExtrude","SWEPT_BODY",BODY,{"disambiguationData":[OSD([sQuery(id+"F2.wireOp",EDGE,"E30.0"),sQuery(id+"F2.wireOp",EDGE,"ktQJATyX-SdxZ-rI7u-VDDm-4vrzMGlF9boW"),sQuery(id+"F2.wireOp",EDGE,"HHLsh4HS-uaBy-oQPs-1Epk-ZBBctw4owGZm"),sQuery(id+"F2.wireOp",EDGE,"51925430-38b8-44a9-8ce9-339719db00ad.filletArc")])]}),"instanceName":"46"});
            var Q47;
            Q47=makeQuery(id+"F4.opPattern","COPY",BODY,{"derivedFrom":makeQuery(id+"F3.opExtrude","SWEPT_BODY",BODY,{"disambiguationData":[OSD([sQuery(id+"F2.wireOp",EDGE,"E30.0"),sQuery(id+"F2.wireOp",EDGE,"ktQJATyX-SdxZ-rI7u-VDDm-4vrzMGlF9boW"),sQuery(id+"F2.wireOp",EDGE,"HHLsh4HS-uaBy-oQPs-1Epk-ZBBctw4owGZm"),sQuery(id+"F2.wireOp",EDGE,"51925430-38b8-44a9-8ce9-339719db00ad.filletArc")])]}),"instanceName":"47"});
            var Q48;
            Q48=makeQuery(id+"F4.opPattern","COPY",BODY,{"derivedFrom":makeQuery(id+"F3.opExtrude","SWEPT_BODY",BODY,{"disambiguationData":[OSD([sQuery(id+"F2.wireOp",EDGE,"E30.0"),sQuery(id+"F2.wireOp",EDGE,"ktQJATyX-SdxZ-rI7u-VDDm-4vrzMGlF9boW"),sQuery(id+"F2.wireOp",EDGE,"HHLsh4HS-uaBy-oQPs-1Epk-ZBBctw4owGZm"),sQuery(id+"F2.wireOp",EDGE,"51925430-38b8-44a9-8ce9-339719db00ad.filletArc")])]}),"instanceName":"48"});
            var Q49;
            Q49=makeQuery(id+"F4.opPattern","COPY",BODY,{"derivedFrom":makeQuery(id+"F3.opExtrude","SWEPT_BODY",BODY,{"disambiguationData":[OSD([sQuery(id+"F2.wireOp",EDGE,"E30.0"),sQuery(id+"F2.wireOp",EDGE,"ktQJATyX-SdxZ-rI7u-VDDm-4vrzMGlF9boW"),sQuery(id+"F2.wireOp",EDGE,"HHLsh4HS-uaBy-oQPs-1Epk-ZBBctw4owGZm"),sQuery(id+"F2.wireOp",EDGE,"51925430-38b8-44a9-8ce9-339719db00ad.filletArc")])]}),"instanceName":"49"});
            var Q50;
            Q50=makeQuery(id+"F1.opRevolve","SWEPT_BODY",BODY,{"disambiguationData":[OSD([sQuery(id+"F0.wireOp",EDGE,"E1"),sQuery(id+"F0.wireOp",EDGE,"E2"),sQuery(id+"F0.wireOp",EDGE,"E3"),sQuery(id+"F0.wireOp",EDGE,"E4"),sQuery(id+"F0.wireOp",EDGE,"E5"),sQuery(id+"F0.wireOp",EDGE,"E6"),sQuery(id+"F0.wireOp",EDGE,"E7"),sQuery(id+"F0.wireOp",EDGE,"E8.MirrorCS"),sQuery(id+"F0.wireOp",EDGE,"E9.MirrorCS"),sQuery(id+"F0.wireOp",EDGE,"E10.MirrorCS"),sQuery(id+"F0.wireOp",EDGE,"E11.MirrorCS"),sQuery(id+"F0.wireOp",EDGE,"E12.MirrorCS"),sQuery(id+"F0.wireOp",EDGE,"E13.MirrorCS"),sQuery(id+"F0.wireOp",EDGE,"E14.MirrorCS")])]});
            booleanBodies(context, id + "F5", {"operationType" : BooleanOperationType.SUBTRACTION, "tools" : qUnion([Q0, Q1, Q2, Q3, Q4, Q5, Q6, Q7, Q8, Q9, Q10, Q11, Q12, Q13, Q14, Q15, Q16, Q17, Q18, Q19, Q20, Q21, Q22, Q23, Q24, Q25, Q26, Q27, Q28, Q29, Q30, Q31, Q32, Q33, Q34, Q35, Q36, Q37, Q38, Q39, Q40, Q41, Q42, Q43, Q44, Q45, Q46, Q47, Q48, Q49]), "targets" : qUnion([Q50])});
        }
    });
